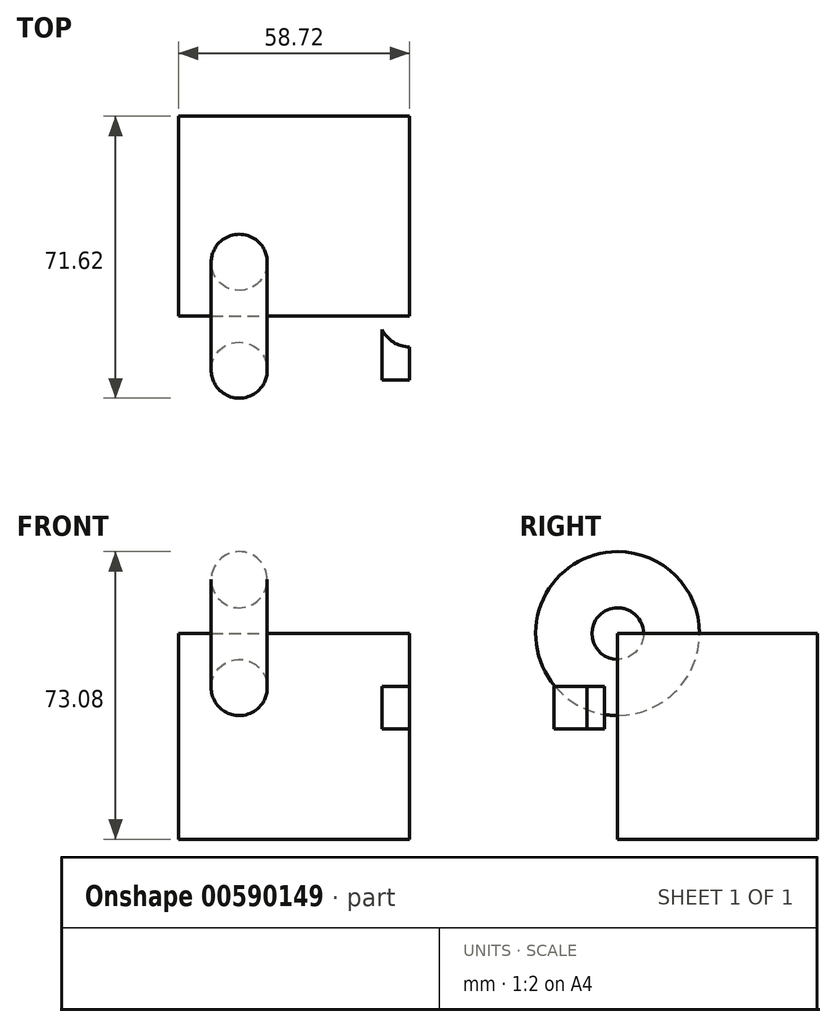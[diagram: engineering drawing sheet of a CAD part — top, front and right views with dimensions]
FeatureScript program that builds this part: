
annotation { "Feature Type Name" : "Feature", "Feature Type Description" : "" }
export const myFeature = defineFeature(function(context is Context, id is Id, definition is map)
    precondition{}
    {
        {
            var Q0;
            Q0=qCreatedBy(makeId("Front.planeOp"),FACE);
            var sketch = newSketch(context, id + "F0", { "sketchPlane" : qUnion([Q0])});
            skLineSegment(sketch, "E0.bottom", {"start": v(0, 62.38) * mm, "end": v(58.72, 62.38) * mm});
            skLineSegment(sketch, "E0.top", {"start": v(0, 10.12) * mm, "end": v(58.72, 10.12) * mm});
            skLineSegment(sketch, "E0.left", {"start": v(0, 62.38) * mm, "end": v(0, 10.12) * mm});
            skLineSegment(sketch, "E0.right", {"start": v(58.72, 62.38) * mm, "end": v(58.72, 10.12) * mm});
            skSolve(sketch);
        }
        {
            var Q0;
            Q0 = qSketchRegion(id + "F0", true);
            extrude(context, id + "F1", {"entities" : qUnion([Q0]), "depth" : 50.8 * mm, "offsetDistance" : 25.4 * mm});
        }
        {
            var Q0;
            Q0=makeQuery(id+"F1.opExtrude","CAP_FACE",FACE,{"disambiguationData":[OSD([sQuery(id+"F0.wireOp",EDGE,"E0.bottom"),sQuery(id+"F0.wireOp",EDGE,"E0.top"),sQuery(id+"F0.wireOp",EDGE,"E0.left"),sQuery(id+"F0.wireOp",EDGE,"E0.right")])],"isStart":false});
            var sketch = newSketch(context, id + "F2", { "sketchPlane" : qUnion([Q0])});
            skCircle(sketch, "E1", {"center": v(15.4, 48.7) * mm, "radius": 7.13 * mm});
            skSolve(sketch);
        }
        {
            var Q0;
            Q0=makeQuery(id+"F2.imprint","IMPRINT",FACE,{"disambiguationData":[TD([[makeQuery(id+"F2.imprint","IMPRINT",EDGE,{"derivedFrom":sQuery(id+"F2.wireOp",EDGE,"E1")}),1.0]])]});
            var Q1;
            Q1=makeQuery(id+"F1.opExtrude","CAP_EDGE",EDGE,{"disambiguationData":[OSD([sQuery(id+"F0.wireOp",EDGE,"E0.bottom")])],"isStart":false});
            revolve(context, id + "F3", {"entities" : qUnion([Q0]), "axis" : qUnion([Q1]), "revolveType" : RevolveType.FULL});
        }
        {
            var Q0;
            Q0=makeQuery(id+"F1.opExtrude","CAP_FACE",FACE,{"disambiguationData":[OSD([sQuery(id+"F0.wireOp",EDGE,"E0.bottom"),sQuery(id+"F0.wireOp",EDGE,"E0.top"),sQuery(id+"F0.wireOp",EDGE,"E0.left"),sQuery(id+"F0.wireOp",EDGE,"E0.right")])],"isStart":false});
            var sketch = newSketch(context, id + "F4", { "sketchPlane" : qUnion([Q0])});
            skLineSegment(sketch, "E2.bottom", {"start": v(41.07, 49) * mm, "end": v(50.9, 49) * mm});
            skLineSegment(sketch, "E2.top", {"start": v(41.07, 38.18) * mm, "end": v(50.9, 38.18) * mm});
            skLineSegment(sketch, "E2.left", {"start": v(41.07, 49) * mm, "end": v(41.07, 38.18) * mm});
            skLineSegment(sketch, "E2.right", {"start": v(50.9, 49) * mm, "end": v(50.9, 38.18) * mm});
            skSolve(sketch);
        }
        {
            var Q0;
            Q0=makeQuery(id+"F4.imprint","IMPRINT",FACE,{"disambiguationData":[TD([[makeQuery(id+"F4.imprint","IMPRINT",EDGE,{"derivedFrom":sQuery(id+"F4.wireOp",EDGE,"E2.bottom")}),-1.0]])]});
            var Q1;
            Q1=makeQuery(id+"F1.opExtrude","CAP_EDGE",EDGE,{"disambiguationData":[OSD([sQuery(id+"F0.wireOp",EDGE,"E0.right")])],"isStart":false});
            revolve(context, id + "F5", {"entities" : qUnion([Q0]), "axis" : qUnion([Q1]), "revolveType" : RevolveType.FULL});
        }
        {
            var Q0;
            Q0=makeQuery(id+"F1.opExtrude","SWEPT_FACE",FACE,{"disambiguationData":[OSD([sQuery(id+"F0.wireOp",EDGE,"E0.bottom")])]});
            var sketch = newSketch(context, id + "F6", { "sketchPlane" : qUnion([Q0])});
            skCircle(sketch, "E3", {"center": v(37.3, -19.66) * mm, "radius": 6.28 * mm});
            skSolve(sketch);
        }
        {
            var Q0;
            Q0=makeQuery(id+"F6.imprint","IMPRINT",FACE,{"disambiguationData":[TD([[makeQuery(id+"F6.imprint","IMPRINT",EDGE,{"derivedFrom":sQuery(id+"F6.wireOp",EDGE,"E3")}),1.0]])]});
            var Q1;
            Q1=makeQuery(id+"F1.opExtrude","SWEPT_EDGE",EDGE,{"disambiguationData":[OSD([sQuery(id+"F0.wireOp",EDGE,"E0.bottom"),sQuery(id+"F0.wireOp",EDGE,"E0.right")])]});
            revolve(context, id + "F7", {"entities" : qUnion([Q0]), "axis" : qUnion([Q1]), "revolveType" : RevolveType.FULL});
        }
        {
            var Q0;
            Q0=makeQuery(id+"F7.opRevolve","SWEPT_BODY",BODY,{"disambiguationData":[OSD([sQuery(id+"F6.wireOp",EDGE,"E3")])]});
            var Q1;
            Q1=makeQuery(id+"F3.opRevolve","SWEPT_BODY",BODY,{"disambiguationData":[OSD([sQuery(id+"F2.wireOp",EDGE,"E1")])]});
            booleanBodies(context, id + "F8", {"operationType" : BooleanOperationType.SUBTRACTION, "tools" : qUnion([Q0]), "targets" : qUnion([Q1])});
        }
        {
            var Q0;
            Q0=makeQuery(id+"F5.opRevolve","SWEPT_FACE",FACE,{"disambiguationData":[OSD([sQuery(id+"F4.wireOp",EDGE,"E2.bottom")])]});
            var sketch = newSketch(context, id + "F9", { "sketchPlane" : qUnion([Q0])});
            skLineSegment(sketch, "E4.bottom", {"start": v(51.67, -66.98) * mm, "end": v(58.72, -66.98) * mm});
            skLineSegment(sketch, "E4.top", {"start": v(51.67, -50.8) * mm, "end": v(58.72, -50.8) * mm});
            skLineSegment(sketch, "E4.left", {"start": v(51.67, -66.98) * mm, "end": v(51.67, -50.8) * mm});
            skLineSegment(sketch, "E4.right", {"start": v(58.72, -66.98) * mm, "end": v(58.72, -50.8) * mm});
            skSolve(sketch);
        }
        {
            var Q0;
            Q0 = qSketchRegion(id + "F9", true);
            extrude(context, id + "F10", {"entities" : qUnion([Q0]), "endBound" : BoundingType.SYMMETRIC, "depth" : 25.4 * mm, "offsetDistance" : 25.4 * mm});
        }
        {
            var Q0;
            Q0=makeQuery(id+"F10.opExtrude","SWEPT_BODY",BODY,{"disambiguationData":[OSD([sQuery(id+"F9.wireOp",EDGE,"E4.bottom"),sQuery(id+"F9.wireOp",EDGE,"E4.top"),sQuery(id+"F9.wireOp",EDGE,"E4.left"),sQuery(id+"F9.wireOp",EDGE,"E4.right")])]});
            var Q1;
            Q1=makeQuery(id+"F5.opRevolve","SWEPT_BODY",BODY,{"disambiguationData":[OSD([sQuery(id+"F4.wireOp",EDGE,"E2.bottom"),sQuery(id+"F4.wireOp",EDGE,"E2.top"),sQuery(id+"F4.wireOp",EDGE,"E2.left"),sQuery(id+"F4.wireOp",EDGE,"E2.right")])]});
            booleanBodies(context, id + "F11", {"operationType" : BooleanOperationType.INTERSECTION, "tools" : qUnion([Q0, Q1])});
        }
    });
